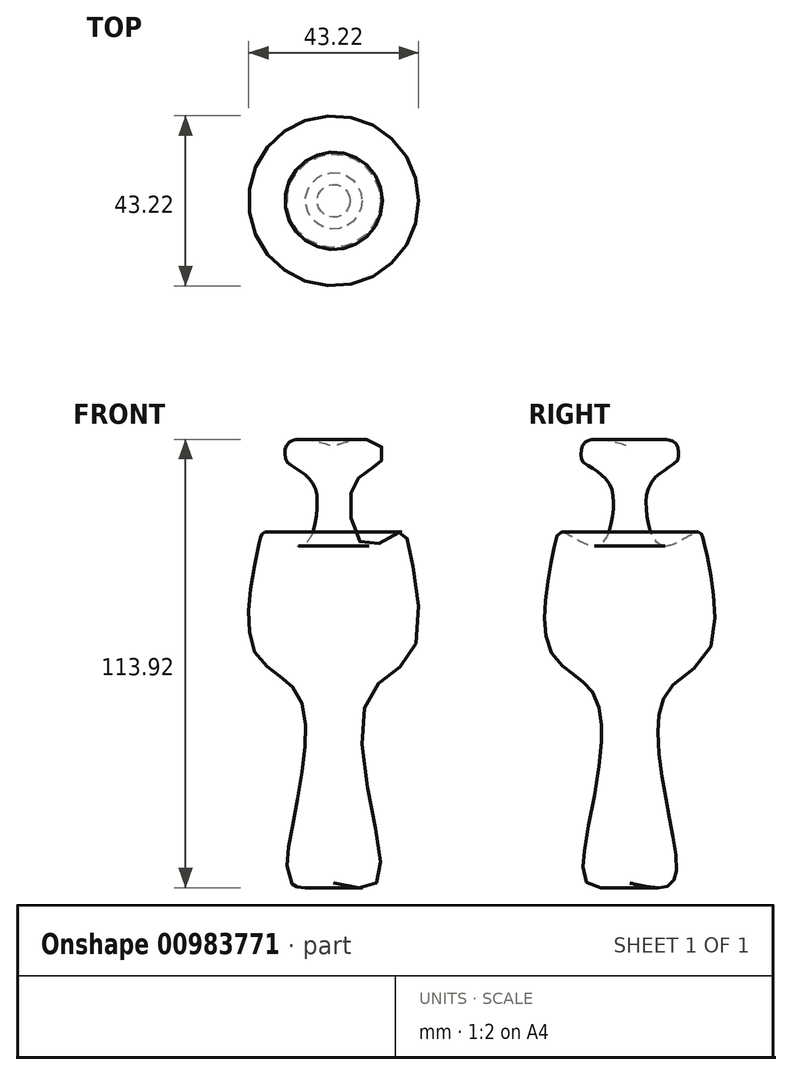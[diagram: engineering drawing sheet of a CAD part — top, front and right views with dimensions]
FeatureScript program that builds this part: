
annotation { "Feature Type Name" : "Feature", "Feature Type Description" : "" }
export const myFeature = defineFeature(function(context is Context, id is Id, definition is map)
    precondition{}
    {
        {
            var Q0;
            Q0=qCreatedBy(makeId("Front.planeOp"),FACE);
            var sketch = newSketch(context, id + "F0", { "sketchPlane" : qUnion([Q0])});
            skLineSegment(sketch, "E0", {"start": v(0, 65.76) * mm, "end": v(0, -63.17) * mm});
            skFitSpline(sketch, "E1", {"points": [v(0, -47.92) * mm, v(10.5, -48.2) * mm, v(10.22, -32.1) * mm, v(9.07, 0) * mm, v(20.3, 11.37) * mm, v(18.85, 38.7) * mm, v(17.12, 41.3) * mm, v(8.2, 37.85) * mm, v(4.17, 49.07) * mm, v(6.76, 55.4) * mm, v(11.66, 58.86) * mm, v(12.23, 59.72) * mm, v(11.37, 64.04) * mm, v(2.16, 63.75) * mm, v(0, 62.89) * mm], "startDerivative": vector(171.1, -39.56) * mm, "endDerivative": vector(-41.99, -21.6) * mm});
            skSolve(sketch);
        }
        {
            var Q0;
            {var subQ0=sQuery(id+"F0.wireOp",EDGE,"E1");Q0=makeQuery(id+"F0.imprint","IMPRINT",FACE,{"disambiguationData":[TD([[makeQuery(id+"F0.imprint","IMPRINT",EDGE,{"derivedFrom":subQ0}),1.0]])]});}
            var Q1;
            Q1=sQuery(id+"F0.wireOp",EDGE,"E0");
            revolve(context, id + "F1", {"surfaceOperationType" : NewSurfaceOperationType.NEW, "entities" : qUnion([Q0]), "axis" : qUnion([Q1]), "revolveType" : RevolveType.FULL});
        }
    });
